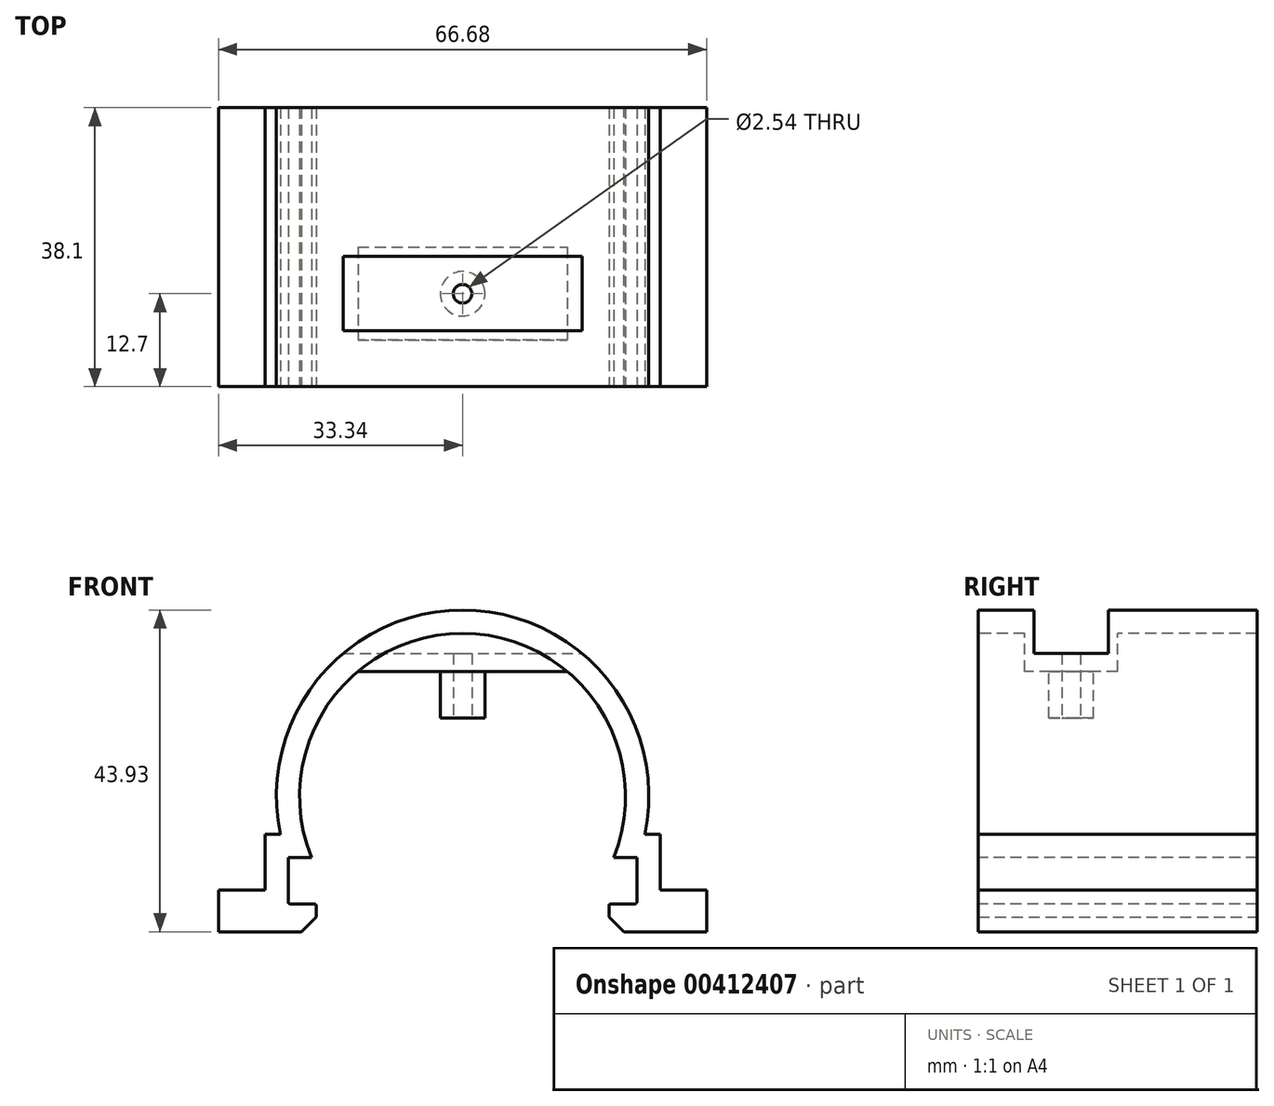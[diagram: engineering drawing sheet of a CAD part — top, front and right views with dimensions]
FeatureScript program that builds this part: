
annotation { "Feature Type Name" : "Feature", "Feature Type Description" : "" }
export const myFeature = defineFeature(function(context is Context, id is Id, definition is map)
    precondition{}
    {
        {
            var Q0;
            Q0=qCreatedBy(makeId("Front.planeOp"),FACE);
            var sketch = newSketch(context, id + "F0", { "sketchPlane" : qUnion([Q0])});
            skLineSegment(sketch, "E0", {"start": v(-23.81, 0) * mm, "end": v(-20.64, 0) * mm});
            skLineSegment(sketch, "E1", {"start": v(0, 0) * mm, "end": v(0, 25.4) * mm, "construction": true});
            skLineSegment(sketch, "E2", {"start": v(-14.29, 25.4) * mm, "end": v(14.29, 25.4) * mm});
            skLineSegment(sketch, "E3", {"start": v(-23.81, 0) * mm, "end": v(-20.64, 0) * mm, "construction": true});
            skLineSegment(sketch, "E4", {"start": v(23.81, 0) * mm, "end": v(20.64, 0) * mm, "construction": true});
            skArc(sketch, "E5", {"start": v(-14.29, 25.4) * mm, "mid": v(-21.6, 13.73) * mm, "end": v(-20.64, 0) * mm});
            skLineSegment(sketch, "E6", {"start": v(-23.81, 0) * mm, "end": v(-23.81, -6.35) * mm});
            skLineSegment(sketch, "E7", {"start": v(23.81, 0) * mm, "end": v(23.81, -6.35) * mm});
            skArc(sketch, "E8.0", {"start": v(-16.33, 27.83) * mm, "mid": v(-24.02, 16.69) * mm, "end": v(-24.9, 3.18) * mm});
            skLineSegment(sketch, "E9", {"start": v(-16.33, 27.83) * mm, "end": v(16.33, 27.83) * mm});
            skLineSegment(sketch, "E10", {"start": v(-26.99, -4.45) * mm, "end": v(-26.99, 3.17) * mm});
            skLineSegment(sketch, "E11", {"start": v(-26.99, 3.17) * mm, "end": v(-24.9, 3.17) * mm});
            skLineSegment(sketch, "E12", {"start": v(26.99, -4.45) * mm, "end": v(26.99, 3.18) * mm});
            skLineSegment(sketch, "E13", {"start": v(26.99, 3.18) * mm, "end": v(24.9, 3.18) * mm});
            skArc(sketch, "E14.trimOffspring", {"start": v(24.9, 3.18) * mm, "mid": v(24.02, 16.69) * mm, "end": v(16.33, 27.83) * mm});
            skArc(sketch, "E15.trimOffspring", {"start": v(20.64, 0) * mm, "mid": v(21.6, 13.73) * mm, "end": v(14.29, 25.4) * mm});
            skLineSegment(sketch, "E16.trimOffspring", {"start": v(20.64, 0) * mm, "end": v(23.81, 0) * mm});
            skLineSegment(sketch, "E17", {"start": v(-23.81, -6.35) * mm, "end": v(-20, -6.35) * mm});
            skLineSegment(sketch, "E18", {"start": v(23.81, -6.35) * mm, "end": v(20, -6.35) * mm});
            skLineSegment(sketch, "E19", {"start": v(-26.99, -4.45) * mm, "end": v(-33.34, -4.45) * mm});
            skLineSegment(sketch, "E20", {"start": v(26.99, -4.45) * mm, "end": v(33.34, -4.45) * mm});
            skLineSegment(sketch, "E21", {"start": v(-33.34, -4.45) * mm, "end": v(-33.34, -10.16) * mm});
            skLineSegment(sketch, "E22", {"start": v(33.34, -4.45) * mm, "end": v(33.34, -10.16) * mm});
            skLineSegment(sketch, "E23", {"start": v(-20, -6.35) * mm, "end": v(-20, -10.16) * mm});
            skLineSegment(sketch, "E24", {"start": v(20, -6.35) * mm, "end": v(20, -10.16) * mm});
            skLineSegment(sketch, "E25", {"start": v(-20, -10.16) * mm, "end": v(-33.34, -10.16) * mm});
            skLineSegment(sketch, "E26", {"start": v(20, -10.16) * mm, "end": v(33.34, -10.16) * mm});
            skSolve(sketch);
        }
        {
            var Q0;
            Q0=makeQuery(id+"F0.imprint","IMPRINT",FACE,{"disambiguationData":[TD([[makeQuery(id+"F0.imprint","IMPRINT",EDGE,{"derivedFrom":sQuery(id+"F0.wireOp",EDGE,"E0")}),1.0]])]});
            extrude(context, id + "F1", {"entities" : qUnion([Q0]), "oppositeDirection" : true, "depth" : 12.7 * mm});
        }
        {
            var Q0;
            Q0=makeQuery(id+"F1.opExtrude","SWEPT_FACE",FACE,{"disambiguationData":[OSD([sQuery(id+"F0.wireOp",EDGE,"E2")])]});
            var sketch = newSketch(context, id + "F2", { "sketchPlane" : qUnion([Q0])});
            skLineSegment(sketch, "E27", {"start": v(0, -12.7) * mm, "end": v(0, -6.35) * mm, "construction": true});
            skPoint(sketch, "E27.endSnap0", {"position": v(0, -12.7) * mm});
            skCircle(sketch, "E28", {"center": v(0, -6.35) * mm, "radius": 3.05 * mm});
            skSolve(sketch);
        }
        {
            var Q0;
            Q0=makeQuery(id+"F2.imprint","IMPRINT",FACE,{"disambiguationData":[TD([[makeQuery(id+"F2.imprint","IMPRINT",EDGE,{"derivedFrom":sQuery(id+"F2.wireOp",EDGE,"E28")}),1.0]])]});
            extrude(context, id + "F3", {"entities" : qUnion([Q0]), "operationType" : NewBodyOperationType.ADD, "depth" : 6.35 * mm});
        }
        {
            var Q0;
            Q0=makeQuery(id+"F1.opExtrude","SWEPT_EDGE",EDGE,{"disambiguationData":[OSD([sQuery(id+"F0.wireOp",EDGE,"E17"),sQuery(id+"F0.wireOp",EDGE,"sQ2Dt9HJ-DLmy-fobY-wEzB-knzwlTL04auf")])]});
            var Q1;
            Q1=makeQuery(id+"F1.opExtrude","SWEPT_EDGE",EDGE,{"disambiguationData":[OSD([sQuery(id+"F0.wireOp",EDGE,"E18"),sQuery(id+"F0.wireOp",EDGE,"bWk3n836-9KEs-FhVF-pOS5-eo05tRzIyBKB")])]});
            fillet(context, id + "F4", {"entities" : qUnion([Q0, Q1]), "radius" : 0.25 * mm, "tangentPropagation" : true, "allowEdgeOverflow" : false});
        }
        {
            var Q0;
            Q0=makeQuery(id+"F1.opExtrude","SWEPT_EDGE",EDGE,{"disambiguationData":[OSD([sQuery(id+"F0.wireOp",EDGE,"E24"),sQuery(id+"F0.wireOp",EDGE,"E26")])]});
            chamfer(context, id + "F5", {"entities" : qUnion([Q0]), "width" : 2.03 * mm, "tangentPropagation" : true});
        }
        {
            var Q0;
            {var subQ0=sQuery(id+"F0.wireOp",EDGE,"E25");var subQ1=sQuery(id+"F0.wireOp",EDGE,"E23");Q0=makeQuery(id+"FkChHWSdqDV76BH_1.boolean.opBoolean","MERGE",EDGE,{"derivedFrom":[makeQuery(id+"F1.opExtrude","SWEPT_EDGE",EDGE,{"disambiguationData":[OSD([subQ1,subQ0])]}),makeQuery(id+"FkChHWSdqDV76BH_1.opExtrude","SWEPT_EDGE",EDGE,{"disambiguationData":[OSD([subQ1,subQ0])]})]});}
            chamfer(context, id + "F6", {"entities" : qUnion([Q0]), "width" : 2.03 * mm, "tangentPropagation" : true});
        }
        {
            var Q0;
            Q0=makeQuery(id+"F3.opExtrude","CAP_FACE",FACE,{"disambiguationData":[OSD([sQuery(id+"F2.wireOp",EDGE,"E28")])],"isStart":false});
            var sketch = newSketch(context, id + "F7", { "sketchPlane" : qUnion([Q0])});
            skCircle(sketch, "E29", {"center": v(0, -6.35) * mm, "radius": 1.27 * mm});
            skSolve(sketch);
        }
        {
            var Q0;
            Q0=makeQuery(id+"F7.imprint","IMPRINT",FACE,{"disambiguationData":[TD([[makeQuery(id+"F7.imprint","IMPRINT",EDGE,{"derivedFrom":sQuery(id+"F7.wireOp",EDGE,"E29")}),1.0]])]});
            extrude(context, id + "F8", {"entities" : qUnion([Q0]), "operationType" : NewBodyOperationType.REMOVE, "endBound" : BoundingType.UP_TO_NEXT, "oppositeDirection" : true, "depth" : 25.4 * mm});
        }
        {
            var Q0;
            Q0=makeQuery(id+"F1.opExtrude","CAP_FACE",FACE,{"disambiguationData":[OSD([sQuery(id+"F0.wireOp",EDGE,"E0"),sQuery(id+"F0.wireOp",EDGE,"E2"),sQuery(id+"F0.wireOp",EDGE,"E5"),sQuery(id+"F0.wireOp",EDGE,"E6"),sQuery(id+"F0.wireOp",EDGE,"E7"),sQuery(id+"F0.wireOp",EDGE,"E8.0"),sQuery(id+"F0.wireOp",EDGE,"E9"),sQuery(id+"F0.wireOp",EDGE,"E10"),sQuery(id+"F0.wireOp",EDGE,"E11"),sQuery(id+"F0.wireOp",EDGE,"E12"),sQuery(id+"F0.wireOp",EDGE,"E13"),sQuery(id+"F0.wireOp",EDGE,"E14.trimOffspring"),sQuery(id+"F0.wireOp",EDGE,"E15.trimOffspring"),sQuery(id+"F0.wireOp",EDGE,"E16.trimOffspring"),sQuery(id+"F0.wireOp",EDGE,"E17"),sQuery(id+"F0.wireOp",EDGE,"E18"),sQuery(id+"F0.wireOp",EDGE,"E19"),sQuery(id+"F0.wireOp",EDGE,"E20"),sQuery(id+"F0.wireOp",EDGE,"E21"),sQuery(id+"F0.wireOp",EDGE,"E22"),sQuery(id+"F0.wireOp",EDGE,"E23"),sQuery(id+"F0.wireOp",EDGE,"E24"),sQuery(id+"F0.wireOp",EDGE,"E25"),sQuery(id+"F0.wireOp",EDGE,"E26")])],"isStart":true});
            var sketch = newSketch(context, id + "F9", { "sketchPlane" : qUnion([Q0])});
            skArc(sketch, "E30", {"start": v(20.64, 0) * mm, "mid": v(0, 30.6) * mm, "end": v(-20.64, 0) * mm});
            skPoint(sketch, "E30.first.point", {"position": v(-14.29, 25.4) * mm});
            skPoint(sketch, "E30.second.point", {"position": v(-20.64, 0) * mm});
            skPoint(sketch, "E30.third.point", {"position": v(20.64, 0) * mm});
            skArc(sketch, "E31", {"start": v(24.9, 3.18) * mm, "mid": v(0, 33.77) * mm, "end": v(-24.9, 3.18) * mm});
            skPoint(sketch, "E31.first.point", {"position": v(-16.33, 27.83) * mm});
            skPoint(sketch, "E31.second.point", {"position": v(-24.9, 3.17) * mm});
            skPoint(sketch, "E31.third.point", {"position": v(24.9, 3.18) * mm});
            skLineSegment(sketch, "E32", {"start": v(-20.64, 0) * mm, "end": v(-24.03, 0) * mm});
            skLineSegment(sketch, "E33", {"start": v(20.64, 0) * mm, "end": v(24.03, 0) * mm});
            skSolve(sketch);
        }
        {
            var Q0;
            {var subQ0=sQuery(id+"F9.wireOp",EDGE,"E30");var subQ1=makeQuery(id+"F1.opExtrude","CAP_EDGE",EDGE,{"disambiguationData":[OSD([sQuery(id+"F0.wireOp",EDGE,"E9")])],"isStart":true});var subQ2=makeQuery(id+"F9.imprint","INTERSECT",VERTEX,{"disambiguationData":[OD(0.0)],"derivedFrom":[subQ1,subQ0]});Q0=makeQuery(id+"F9.imprint","IMPRINT",FACE,{"disambiguationData":[TD([[makeQuery(id+"F9.imprint","IMPRINT",EDGE,{"disambiguationData":[TD([[subQ2,-1.0]])],"derivedFrom":subQ0}),-1.0]])]});}
            var Q1;
            {var subQ6=sQuery(id+"F0.wireOp",EDGE,"E12");Q1=makeQuery(id+"F9.imprint","IMPRINT",FACE,{"disambiguationData":[TD([[makeQuery(id+"F9.imprint","IMPRINT",EDGE,{"derivedFrom":makeQuery(id+"F1.opExtrude","CAP_EDGE",EDGE,{"disambiguationData":[OSD([subQ6])],"isStart":true})}),1.0]])]});}
            var Q2;
            {var subQ6=sQuery(id+"F0.wireOp",EDGE,"E10");Q2=makeQuery(id+"F9.imprint","IMPRINT",FACE,{"disambiguationData":[TD([[makeQuery(id+"F9.imprint","IMPRINT",EDGE,{"derivedFrom":makeQuery(id+"F1.opExtrude","CAP_EDGE",EDGE,{"disambiguationData":[OSD([subQ6])],"isStart":true})}),-1.0]])]});}
            extrude(context, id + "F10", {"entities" : qUnion([Q0, Q1, Q2]), "operationType" : NewBodyOperationType.ADD, "depth" : 6.35 * mm});
        }
        {
            var Q0;
            Q0=makeQuery(id+"F1.opExtrude","CAP_FACE",FACE,{"disambiguationData":[OSD([sQuery(id+"F0.wireOp",EDGE,"E0"),sQuery(id+"F0.wireOp",EDGE,"E2"),sQuery(id+"F0.wireOp",EDGE,"E5"),sQuery(id+"F0.wireOp",EDGE,"E6"),sQuery(id+"F0.wireOp",EDGE,"E7"),sQuery(id+"F0.wireOp",EDGE,"E8.0"),sQuery(id+"F0.wireOp",EDGE,"E9"),sQuery(id+"F0.wireOp",EDGE,"E10"),sQuery(id+"F0.wireOp",EDGE,"E11"),sQuery(id+"F0.wireOp",EDGE,"E12"),sQuery(id+"F0.wireOp",EDGE,"E13"),sQuery(id+"F0.wireOp",EDGE,"E14.trimOffspring"),sQuery(id+"F0.wireOp",EDGE,"E15.trimOffspring"),sQuery(id+"F0.wireOp",EDGE,"E16.trimOffspring"),sQuery(id+"F0.wireOp",EDGE,"E17"),sQuery(id+"F0.wireOp",EDGE,"E18"),sQuery(id+"F0.wireOp",EDGE,"E19"),sQuery(id+"F0.wireOp",EDGE,"E20"),sQuery(id+"F0.wireOp",EDGE,"E21"),sQuery(id+"F0.wireOp",EDGE,"E22"),sQuery(id+"F0.wireOp",EDGE,"E23"),sQuery(id+"F0.wireOp",EDGE,"E24"),sQuery(id+"F0.wireOp",EDGE,"E25"),sQuery(id+"F0.wireOp",EDGE,"E26")])],"isStart":false});
            var sketch = newSketch(context, id + "F11", { "sketchPlane" : qUnion([Q0])});
            skArc(sketch, "E34", {"start": v(20.64, 0) * mm, "mid": v(0, 30.6) * mm, "end": v(-20.64, 0) * mm});
            skPoint(sketch, "E34.first.point", {"position": v(-14.29, 25.4) * mm});
            skPoint(sketch, "E34.second.point", {"position": v(-20.64, 0) * mm});
            skPoint(sketch, "E34.third.point", {"position": v(20.64, 0) * mm});
            skArc(sketch, "E35", {"start": v(24.9, 3.18) * mm, "mid": v(0, 33.77) * mm, "end": v(-24.9, 3.18) * mm});
            skPoint(sketch, "E35.first.point", {"position": v(-16.33, 27.83) * mm});
            skPoint(sketch, "E35.second.point", {"position": v(-24.9, 3.18) * mm});
            skPoint(sketch, "E35.third.point", {"position": v(24.9, 3.17) * mm});
            skSolve(sketch);
        }
        {
            var Q0;
            {var subQ0=sQuery(id+"F11.wireOp",EDGE,"E34");var subQ1=makeQuery(id+"F1.opExtrude","CAP_EDGE",EDGE,{"disambiguationData":[OSD([sQuery(id+"F0.wireOp",EDGE,"E9")])],"isStart":false});var subQ2=makeQuery(id+"F11.imprint","INTERSECT",VERTEX,{"disambiguationData":[OD(0.0)],"derivedFrom":[subQ1,subQ0]});Q0=makeQuery(id+"F11.imprint","IMPRINT",FACE,{"disambiguationData":[TD([[makeQuery(id+"F11.imprint","IMPRINT",EDGE,{"disambiguationData":[TD([[subQ2,-1.0]])],"derivedFrom":subQ0}),-1.0]])]});}
            var Q1;
            {var subQ7=sQuery(id+"F0.wireOp",EDGE,"E12");Q1=makeQuery(id+"F11.imprint","IMPRINT",FACE,{"disambiguationData":[TD([[makeQuery(id+"F11.imprint","IMPRINT",EDGE,{"derivedFrom":makeQuery(id+"F1.opExtrude","CAP_EDGE",EDGE,{"disambiguationData":[OSD([subQ7])],"isStart":false})}),-1.0]])]});}
            var Q2;
            {var subQ11=sQuery(id+"F0.wireOp",EDGE,"E0");var subQ18=makeQuery(id+"F1.opExtrude","CAP_EDGE",EDGE,{"disambiguationData":[OSD([subQ11])],"isStart":false});Q2=makeQuery(id+"F11.imprint","IMPRINT",FACE,{"disambiguationData":[TD([[makeQuery(id+"F11.imprint","IMPRINT",EDGE,{"derivedFrom":subQ18}),-1.0]])]});}
            extrude(context, id + "F12", {"entities" : qUnion([Q0, Q1, Q2]), "operationType" : NewBodyOperationType.ADD, "depth" : 19.05 * mm});
        }
        {
            var Q0;
            Q0=makeQuery(id+"F10.opExtrude","CAP_FACE",FACE,{"disambiguationData":[OSD([sQuery(id+"F0.wireOp",EDGE,"E0"),sQuery(id+"F0.wireOp",EDGE,"E2"),sQuery(id+"F0.wireOp",EDGE,"E5"),sQuery(id+"F0.wireOp",EDGE,"E6"),sQuery(id+"F0.wireOp",EDGE,"E7"),sQuery(id+"F0.wireOp",EDGE,"E8.0"),sQuery(id+"F0.wireOp",EDGE,"E9"),sQuery(id+"F0.wireOp",EDGE,"E10"),sQuery(id+"F0.wireOp",EDGE,"E11"),sQuery(id+"F0.wireOp",EDGE,"E12"),sQuery(id+"F0.wireOp",EDGE,"E13"),sQuery(id+"F0.wireOp",EDGE,"E14.trimOffspring"),sQuery(id+"F0.wireOp",EDGE,"E15.trimOffspring"),sQuery(id+"F0.wireOp",EDGE,"E16.trimOffspring"),sQuery(id+"F0.wireOp",EDGE,"E17"),sQuery(id+"F0.wireOp",EDGE,"E18"),sQuery(id+"F0.wireOp",EDGE,"E19"),sQuery(id+"F0.wireOp",EDGE,"E20"),sQuery(id+"F0.wireOp",EDGE,"E21"),sQuery(id+"F0.wireOp",EDGE,"E22"),sQuery(id+"F0.wireOp",EDGE,"E23"),sQuery(id+"F0.wireOp",EDGE,"E24"),sQuery(id+"F0.wireOp",EDGE,"E25"),sQuery(id+"F0.wireOp",EDGE,"E26"),sQuery(id+"F9.wireOp",EDGE,"E30"),sQuery(id+"F9.wireOp",EDGE,"E31"),sQuery(id+"F9.wireOp",EDGE,"E32"),sQuery(id+"F9.wireOp",EDGE,"E33")])],"isStart":true});
            var sketch = newSketch(context, id + "F13", { "sketchPlane" : qUnion([Q0])});
            skLineSegment(sketch, "E36", {"start": v(-16.33, 27.83) * mm, "end": v(16.33, 27.83) * mm});
            skSolve(sketch);
        }
        {
            var Q0;
            {var subQ1=sQuery(id+"F9.wireOp",EDGE,"E31");var subQ2=makeQuery(id+"F10.opExtrude","CAP_EDGE",EDGE,{"disambiguationData":[OSD([subQ1])],"isStart":true});Q0=makeQuery(id+"F13.imprint","IMPRINT",FACE,{"disambiguationData":[TD([[makeQuery(id+"F13.imprint","IMPRINT",EDGE,{"derivedFrom":subQ2}),-1.0]])]});}
            var Q1;
            {var subQ1=sQuery(id+"F0.wireOp",EDGE,"E5");var subQ2=sQuery(id+"F0.wireOp",EDGE,"E15.trimOffspring");var subQ3=sQuery(id+"F9.wireOp",EDGE,"E30");var subQ4=makeQuery(id+"F10.boolean.opBoolean","SPLIT",EDGE,{"disambiguationData":[topologyDisambiguationEdgeConnected([makeQuery(id+"F1.opExtrude","SWEPT_FACE",FACE,{"disambiguationData":[OSD([subQ1])]}),makeQuery(id+"F1.opExtrude","SWEPT_FACE",FACE,{"disambiguationData":[OSD([subQ2])]}),makeQuery(id+"F10.opExtrude","SWEPT_FACE",FACE,{"disambiguationData":[OSD([subQ3])]}),makeQuery(id+"F10.opExtrude","CAP_FACE",FACE,{"disambiguationData":[OSD([sQuery(id+"F0.wireOp",EDGE,"E0"),sQuery(id+"F0.wireOp",EDGE,"E2"),subQ1,sQuery(id+"F0.wireOp",EDGE,"E6"),sQuery(id+"F0.wireOp",EDGE,"E7"),sQuery(id+"F0.wireOp",EDGE,"E8.0"),sQuery(id+"F0.wireOp",EDGE,"E9"),sQuery(id+"F0.wireOp",EDGE,"E10"),sQuery(id+"F0.wireOp",EDGE,"E11"),sQuery(id+"F0.wireOp",EDGE,"E12"),sQuery(id+"F0.wireOp",EDGE,"E13"),sQuery(id+"F0.wireOp",EDGE,"E14.trimOffspring"),subQ2,sQuery(id+"F0.wireOp",EDGE,"E16.trimOffspring"),sQuery(id+"F0.wireOp",EDGE,"E17"),sQuery(id+"F0.wireOp",EDGE,"E18"),sQuery(id+"F0.wireOp",EDGE,"E19"),sQuery(id+"F0.wireOp",EDGE,"E20"),sQuery(id+"F0.wireOp",EDGE,"E21"),sQuery(id+"F0.wireOp",EDGE,"E22"),sQuery(id+"F0.wireOp",EDGE,"E23"),sQuery(id+"F0.wireOp",EDGE,"E24"),sQuery(id+"F0.wireOp",EDGE,"E25"),sQuery(id+"F0.wireOp",EDGE,"E26"),subQ3,sQuery(id+"F9.wireOp",EDGE,"E31"),sQuery(id+"F9.wireOp",EDGE,"E32"),sQuery(id+"F9.wireOp",EDGE,"E33")])],"isStart":true})])],"derivedFrom":makeQuery(id+"F10.opExtrude","CAP_EDGE",EDGE,{"disambiguationData":[OSD([subQ3])],"isStart":true})});Q1=makeQuery(id+"F13.imprint","IMPRINT",FACE,{"disambiguationData":[TD([[makeQuery(id+"F13.imprint","IMPRINT",EDGE,{"derivedFrom":subQ4}),-1.0]])]});}
            extrude(context, id + "F14", {"entities" : qUnion([Q0, Q1]), "operationType" : NewBodyOperationType.ADD, "depth" : 1.27 * mm});
        }
        {
            var Q0;
            Q0=makeQuery(id+"F12.opExtrude","CAP_FACE",FACE,{"disambiguationData":[OSD([sQuery(id+"F0.wireOp",EDGE,"E0"),sQuery(id+"F0.wireOp",EDGE,"E2"),sQuery(id+"F0.wireOp",EDGE,"E5"),sQuery(id+"F0.wireOp",EDGE,"E6"),sQuery(id+"F0.wireOp",EDGE,"E7"),sQuery(id+"F0.wireOp",EDGE,"E8.0"),sQuery(id+"F0.wireOp",EDGE,"E9"),sQuery(id+"F0.wireOp",EDGE,"E10"),sQuery(id+"F0.wireOp",EDGE,"E11"),sQuery(id+"F0.wireOp",EDGE,"E12"),sQuery(id+"F0.wireOp",EDGE,"E13"),sQuery(id+"F0.wireOp",EDGE,"E14.trimOffspring"),sQuery(id+"F0.wireOp",EDGE,"E15.trimOffspring"),sQuery(id+"F0.wireOp",EDGE,"E16.trimOffspring"),sQuery(id+"F0.wireOp",EDGE,"E17"),sQuery(id+"F0.wireOp",EDGE,"E18"),sQuery(id+"F0.wireOp",EDGE,"E19"),sQuery(id+"F0.wireOp",EDGE,"E20"),sQuery(id+"F0.wireOp",EDGE,"E21"),sQuery(id+"F0.wireOp",EDGE,"E22"),sQuery(id+"F0.wireOp",EDGE,"E23"),sQuery(id+"F0.wireOp",EDGE,"E24"),sQuery(id+"F0.wireOp",EDGE,"E25"),sQuery(id+"F0.wireOp",EDGE,"E26"),sQuery(id+"F11.wireOp",EDGE,"E34"),sQuery(id+"F11.wireOp",EDGE,"E35")])],"isStart":true});
            var sketch = newSketch(context, id + "F15", { "sketchPlane" : qUnion([Q0])});
            skLineSegment(sketch, "E37", {"start": v(-16.33, 27.83) * mm, "end": v(16.33, 27.83) * mm});
            skSolve(sketch);
        }
        {
            var Q0;
            {var subQ1=sQuery(id+"F11.wireOp",EDGE,"E35");var subQ2=makeQuery(id+"F12.opExtrude","CAP_EDGE",EDGE,{"disambiguationData":[OSD([subQ1])],"isStart":true});Q0=makeQuery(id+"F15.imprint","IMPRINT",FACE,{"disambiguationData":[TD([[makeQuery(id+"F15.imprint","IMPRINT",EDGE,{"derivedFrom":subQ2}),-1.0]])]});}
            var Q1;
            {var subQ1=sQuery(id+"F11.wireOp",EDGE,"E34");var subQ2=sQuery(id+"F0.wireOp",EDGE,"E15.trimOffspring");var subQ3=sQuery(id+"F0.wireOp",EDGE,"E5");var subQ4=makeQuery(id+"F12.boolean.opBoolean","SPLIT",EDGE,{"disambiguationData":[topologyDisambiguationEdgeConnected([makeQuery(id+"F1.opExtrude","SWEPT_FACE",FACE,{"disambiguationData":[OSD([subQ3])]}),makeQuery(id+"F1.opExtrude","SWEPT_FACE",FACE,{"disambiguationData":[OSD([subQ2])]}),makeQuery(id+"F10.opExtrude","SWEPT_FACE",FACE,{"disambiguationData":[OSD([sQuery(id+"F9.wireOp",EDGE,"E30")])]}),makeQuery(id+"F12.opExtrude","SWEPT_FACE",FACE,{"disambiguationData":[OSD([subQ1])]}),makeQuery(id+"F12.opExtrude","CAP_FACE",FACE,{"disambiguationData":[OSD([sQuery(id+"F0.wireOp",EDGE,"E0"),sQuery(id+"F0.wireOp",EDGE,"E2"),subQ3,sQuery(id+"F0.wireOp",EDGE,"E6"),sQuery(id+"F0.wireOp",EDGE,"E7"),sQuery(id+"F0.wireOp",EDGE,"E8.0"),sQuery(id+"F0.wireOp",EDGE,"E9"),sQuery(id+"F0.wireOp",EDGE,"E10"),sQuery(id+"F0.wireOp",EDGE,"E11"),sQuery(id+"F0.wireOp",EDGE,"E12"),sQuery(id+"F0.wireOp",EDGE,"E13"),sQuery(id+"F0.wireOp",EDGE,"E14.trimOffspring"),subQ2,sQuery(id+"F0.wireOp",EDGE,"E16.trimOffspring"),sQuery(id+"F0.wireOp",EDGE,"E17"),sQuery(id+"F0.wireOp",EDGE,"E18"),sQuery(id+"F0.wireOp",EDGE,"E19"),sQuery(id+"F0.wireOp",EDGE,"E20"),sQuery(id+"F0.wireOp",EDGE,"E21"),sQuery(id+"F0.wireOp",EDGE,"E22"),sQuery(id+"F0.wireOp",EDGE,"E23"),sQuery(id+"F0.wireOp",EDGE,"E24"),sQuery(id+"F0.wireOp",EDGE,"E25"),sQuery(id+"F0.wireOp",EDGE,"E26"),subQ1,sQuery(id+"F11.wireOp",EDGE,"E35")])],"isStart":true})])],"derivedFrom":makeQuery(id+"F12.opExtrude","CAP_EDGE",EDGE,{"disambiguationData":[OSD([subQ1])],"isStart":true})});Q1=makeQuery(id+"F15.imprint","IMPRINT",FACE,{"disambiguationData":[TD([[makeQuery(id+"F15.imprint","IMPRINT",EDGE,{"derivedFrom":subQ4}),-1.0]])]});}
            extrude(context, id + "F16", {"entities" : qUnion([Q0, Q1]), "operationType" : NewBodyOperationType.ADD, "depth" : 1.27 * mm});
        }
    });
